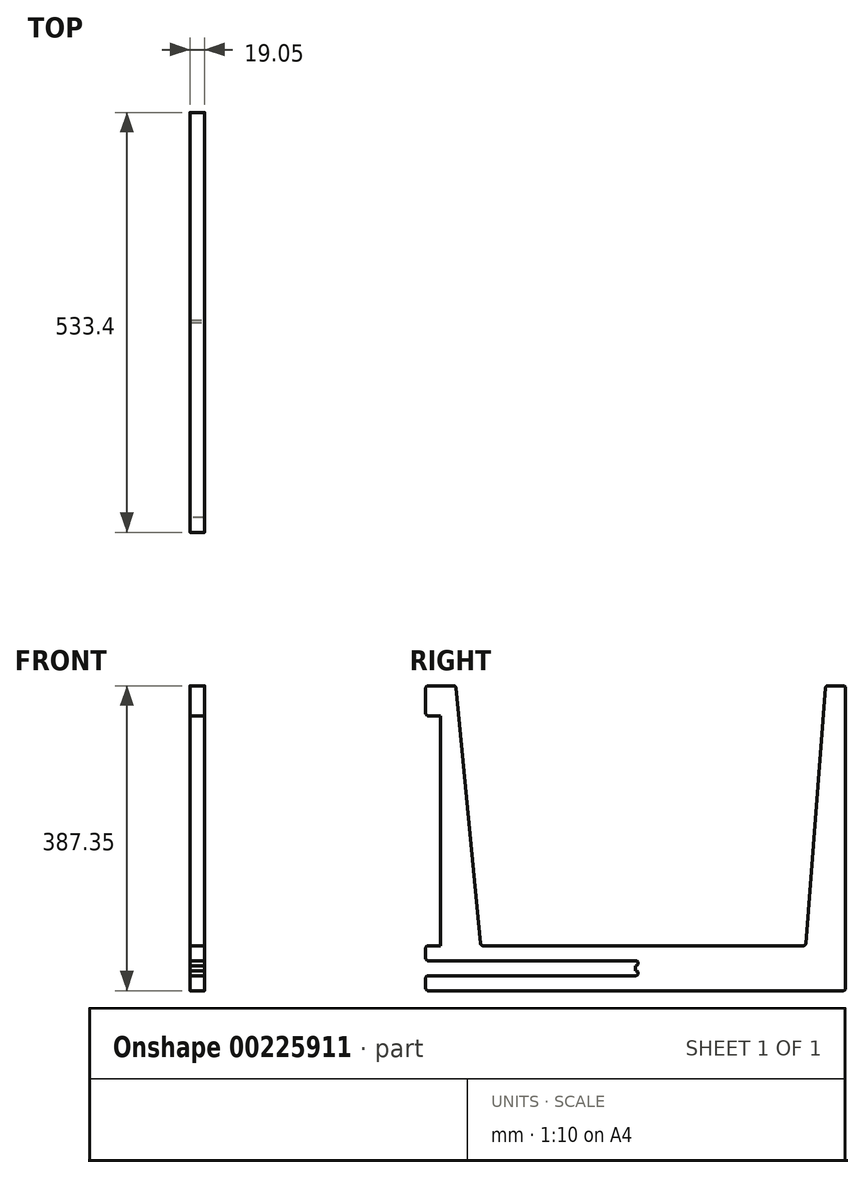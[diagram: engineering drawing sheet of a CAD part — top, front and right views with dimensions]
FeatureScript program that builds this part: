
annotation { "Feature Type Name" : "Feature", "Feature Type Description" : "" }
export const myFeature = defineFeature(function(context is Context, id is Id, definition is map)
    precondition{}
    {
        {
            var Q0;
            Q0=qCreatedBy(makeId("Right.planeOp"),FACE);
            cPlane(context, id + "F0", {"entities" : qUnion([Q0]), "cplaneType" : CPlaneType.OFFSET, "offset" : 19.05 * mm, "width" : 152.4 * mm, "height" : 152.4 * mm});
        }
        {
            var Q0;
            Q0=qCreatedBy(id+"F0.planeOp",FACE);
            var sketch = newSketch(context, id + "F1", { "sketchPlane" : qUnion([Q0])});
            skLineSegment(sketch, "E0", {"start": v(-19.05, 0) * mm, "end": v(-19.05, 19.05) * mm});
            skLineSegment(sketch, "E1", {"start": v(-19.05, 19.05) * mm, "end": v(247.65, 19.05) * mm});
            skLineSegment(sketch, "E2", {"start": v(247.65, 19.05) * mm, "end": v(247.65, 38.1) * mm});
            skLineSegment(sketch, "E3", {"start": v(247.65, 38.1) * mm, "end": v(-19.05, 38.1) * mm});
            skLineSegment(sketch, "E4", {"start": v(-19.05, 38.1) * mm, "end": v(-19.05, 57.15) * mm});
            skLineSegment(sketch, "E5", {"start": v(-19.05, 57.15) * mm, "end": v(0, 57.15) * mm});
            skLineSegment(sketch, "E6", {"start": v(0, 57.15) * mm, "end": v(0, 349.25) * mm});
            skLineSegment(sketch, "E7", {"start": v(0, 349.25) * mm, "end": v(-19.05, 349.25) * mm});
            skLineSegment(sketch, "E8", {"start": v(-19.05, 349.25) * mm, "end": v(-19.05, 387.35) * mm});
            skLineSegment(sketch, "E9", {"start": v(-19.05, 387.35) * mm, "end": v(19.05, 387.35) * mm});
            skLineSegment(sketch, "E10", {"start": v(19.05, 387.35) * mm, "end": v(50.8, 57.15) * mm});
            skLineSegment(sketch, "E11", {"start": v(50.8, 57.15) * mm, "end": v(463.55, 57.15) * mm});
            skLineSegment(sketch, "E12", {"start": v(463.55, 57.15) * mm, "end": v(488.95, 387.35) * mm});
            skLineSegment(sketch, "E13", {"start": v(488.95, 387.35) * mm, "end": v(514.35, 387.35) * mm});
            skLineSegment(sketch, "E14", {"start": v(514.35, 387.35) * mm, "end": v(514.35, 0) * mm});
            skLineSegment(sketch, "E15", {"start": v(514.35, 0) * mm, "end": v(-19.05, 0) * mm});
            skSolve(sketch);
        }
        {
            var Q0;
            Q0 = qSketchRegion(id + "F1", true);
            extrude(context, id + "F2", {"entities" : qUnion([Q0]), "depth" : 19.05 * mm});
        }
        {
            var Q0;
            Q0=makeQuery(id+"F2.opExtrude","SWEPT_EDGE",EDGE,{"disambiguationData":[OSD([sQuery(id+"F1.wireOp",EDGE,"E0"),sQuery(id+"F1.wireOp",EDGE,"E15")])]});
            var Q1;
            Q1=makeQuery(id+"F2.opExtrude","SWEPT_EDGE",EDGE,{"disambiguationData":[OSD([sQuery(id+"F1.wireOp",EDGE,"E0"),sQuery(id+"F1.wireOp",EDGE,"E1")])]});
            var Q2;
            Q2=makeQuery(id+"F2.opExtrude","SWEPT_EDGE",EDGE,{"disambiguationData":[OSD([sQuery(id+"F1.wireOp",EDGE,"E3"),sQuery(id+"F1.wireOp",EDGE,"E4")])]});
            var Q3;
            Q3=makeQuery(id+"F2.opExtrude","SWEPT_EDGE",EDGE,{"disambiguationData":[OSD([sQuery(id+"F1.wireOp",EDGE,"E4"),sQuery(id+"F1.wireOp",EDGE,"E5")])]});
            var Q4;
            Q4=makeQuery(id+"F2.opExtrude","SWEPT_EDGE",EDGE,{"disambiguationData":[OSD([sQuery(id+"F1.wireOp",EDGE,"E7"),sQuery(id+"F1.wireOp",EDGE,"E8")])]});
            var Q5;
            Q5=makeQuery(id+"F2.opExtrude","SWEPT_EDGE",EDGE,{"disambiguationData":[OSD([sQuery(id+"F1.wireOp",EDGE,"E8"),sQuery(id+"F1.wireOp",EDGE,"E9")])]});
            var Q6;
            Q6=makeQuery(id+"F2.opExtrude","SWEPT_EDGE",EDGE,{"disambiguationData":[OSD([sQuery(id+"F1.wireOp",EDGE,"E9"),sQuery(id+"F1.wireOp",EDGE,"E10")])]});
            var Q7;
            Q7=makeQuery(id+"F2.opExtrude","SWEPT_EDGE",EDGE,{"disambiguationData":[OSD([sQuery(id+"F1.wireOp",EDGE,"E10"),sQuery(id+"F1.wireOp",EDGE,"E11")])]});
            var Q8;
            Q8=makeQuery(id+"F2.opExtrude","SWEPT_EDGE",EDGE,{"disambiguationData":[OSD([sQuery(id+"F1.wireOp",EDGE,"E11"),sQuery(id+"F1.wireOp",EDGE,"E12")])]});
            var Q9;
            Q9=makeQuery(id+"F2.opExtrude","SWEPT_EDGE",EDGE,{"disambiguationData":[OSD([sQuery(id+"F1.wireOp",EDGE,"E12"),sQuery(id+"F1.wireOp",EDGE,"E13")])]});
            fillet(context, id + "F3", {"entities" : qUnion([Q0, Q1, Q2, Q3, Q4, Q5, Q6, Q7, Q8, Q9]), "radius" : 3.17 * mm, "tangentPropagation" : true, "allowEdgeOverflow" : false});
        }
        {
            var Q0;
            Q0=makeQuery(id+"F2.opExtrude","CAP_FACE",FACE,{"disambiguationData":[OSD([sQuery(id+"F1.wireOp",EDGE,"E0"),sQuery(id+"F1.wireOp",EDGE,"E1"),sQuery(id+"F1.wireOp",EDGE,"E2"),sQuery(id+"F1.wireOp",EDGE,"E3"),sQuery(id+"F1.wireOp",EDGE,"E4"),sQuery(id+"F1.wireOp",EDGE,"E5"),sQuery(id+"F1.wireOp",EDGE,"E6"),sQuery(id+"F1.wireOp",EDGE,"E7"),sQuery(id+"F1.wireOp",EDGE,"E8"),sQuery(id+"F1.wireOp",EDGE,"E9"),sQuery(id+"F1.wireOp",EDGE,"E10"),sQuery(id+"F1.wireOp",EDGE,"E11"),sQuery(id+"F1.wireOp",EDGE,"E12"),sQuery(id+"F1.wireOp",EDGE,"E13"),sQuery(id+"F1.wireOp",EDGE,"E14"),sQuery(id+"F1.wireOp",EDGE,"E15")])],"isStart":false});
            var sketch = newSketch(context, id + "F4", { "sketchPlane" : qUnion([Q0])});
            skArc(sketch, "E16", {"start": v(247.65, 19.05) * mm, "mid": v(250.83, 22.23) * mm, "end": v(247.65, 25.4) * mm});
            skArc(sketch, "E17", {"start": v(247.65, 38.1) * mm, "mid": v(250.83, 34.93) * mm, "end": v(247.65, 31.75) * mm});
            skLineSegment(sketch, "E18", {"start": v(247.65, 19.05) * mm, "end": v(247.65, 25.4) * mm});
            skLineSegment(sketch, "E19", {"start": v(247.65, 31.75) * mm, "end": v(247.65, 38.1) * mm});
            skSolve(sketch);
        }
        {
            var Q0;
            Q0 = qSketchRegion(id + "F4", true);
            extrude(context, id + "F5", {"entities" : qUnion([Q0]), "operationType" : NewBodyOperationType.REMOVE, "oppositeDirection" : true, "depth" : 19.05 * mm});
        }
        {
            var Q0;
            Q0=makeQuery(id+"F2.opExtrude","SWEPT_EDGE",EDGE,{"disambiguationData":[OSD([sQuery(id+"F1.wireOp",EDGE,"E14"),sQuery(id+"F1.wireOp",EDGE,"E15")])]});
            var Q1;
            Q1=makeQuery(id+"F2.opExtrude","SWEPT_EDGE",EDGE,{"disambiguationData":[OSD([sQuery(id+"F1.wireOp",EDGE,"E13"),sQuery(id+"F1.wireOp",EDGE,"E14")])]});
            fillet(context, id + "F6", {"entities" : qUnion([Q0, Q1]), "radius" : 3.17 * mm, "tangentPropagation" : true, "allowEdgeOverflow" : false});
        }
    });
